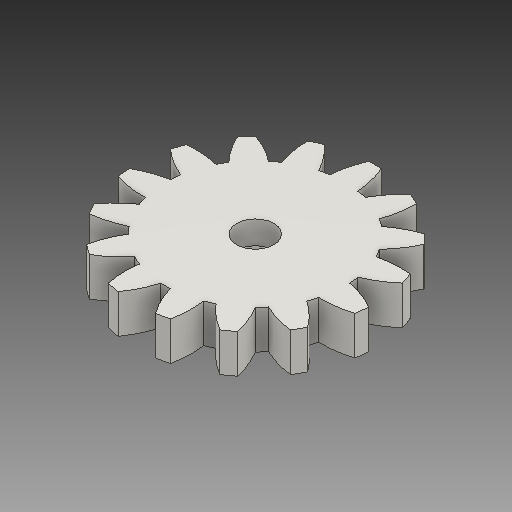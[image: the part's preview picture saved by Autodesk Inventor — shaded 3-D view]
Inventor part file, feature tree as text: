
AUTODESK INVENTOR PART (.ipt)
format: ipt  version: 2018 (Build 220112000, 112)  size: 221,696 bytes
history: native  units: mm
features: other x13, sketch x4, plane x4
ambient origin geometry x8: Origin, YZ Plane, XZ Plane, XY Plane, X Axis, Y Axis, Z Axis, Center Point
bodies: Volumenkörper1 (feature_tree)
feature tree (21):
  other  "Stirnzahnrad2"
  other  "Solid1::Stirnzahnrad2"
  other  "Bezeichnung1"
  sketch  "Sketch1"  dims[d0=10.0mm]
  sketch  "Sketch2"  dims[d16=40.0mm d17=0.0mm d41=0.0mm d43=40.0mm d46=40.0mm d47=0.0mm d48=0.0mm]
  sketch  "Skizze3"
  sketch  "Skizze4"
  plane  "XZ Plane_1"
  plane  "Work Plane2"
  plane  "Work Plane8"
  plane  "Work Plane9"
  other  "Z Axis_1"
  other  "Flä1"
  other  "Srf1::Abgeleitet"
  other  "Abstands-iMate"
  other  "Ausrichtungs-iMate"
  other  "Netz-iMate"
  other  "Achsen-iMate"
  other  "Positions-iMate"
  other  "Netz-iMate 2"
  other  "Startebenen-iMate"
